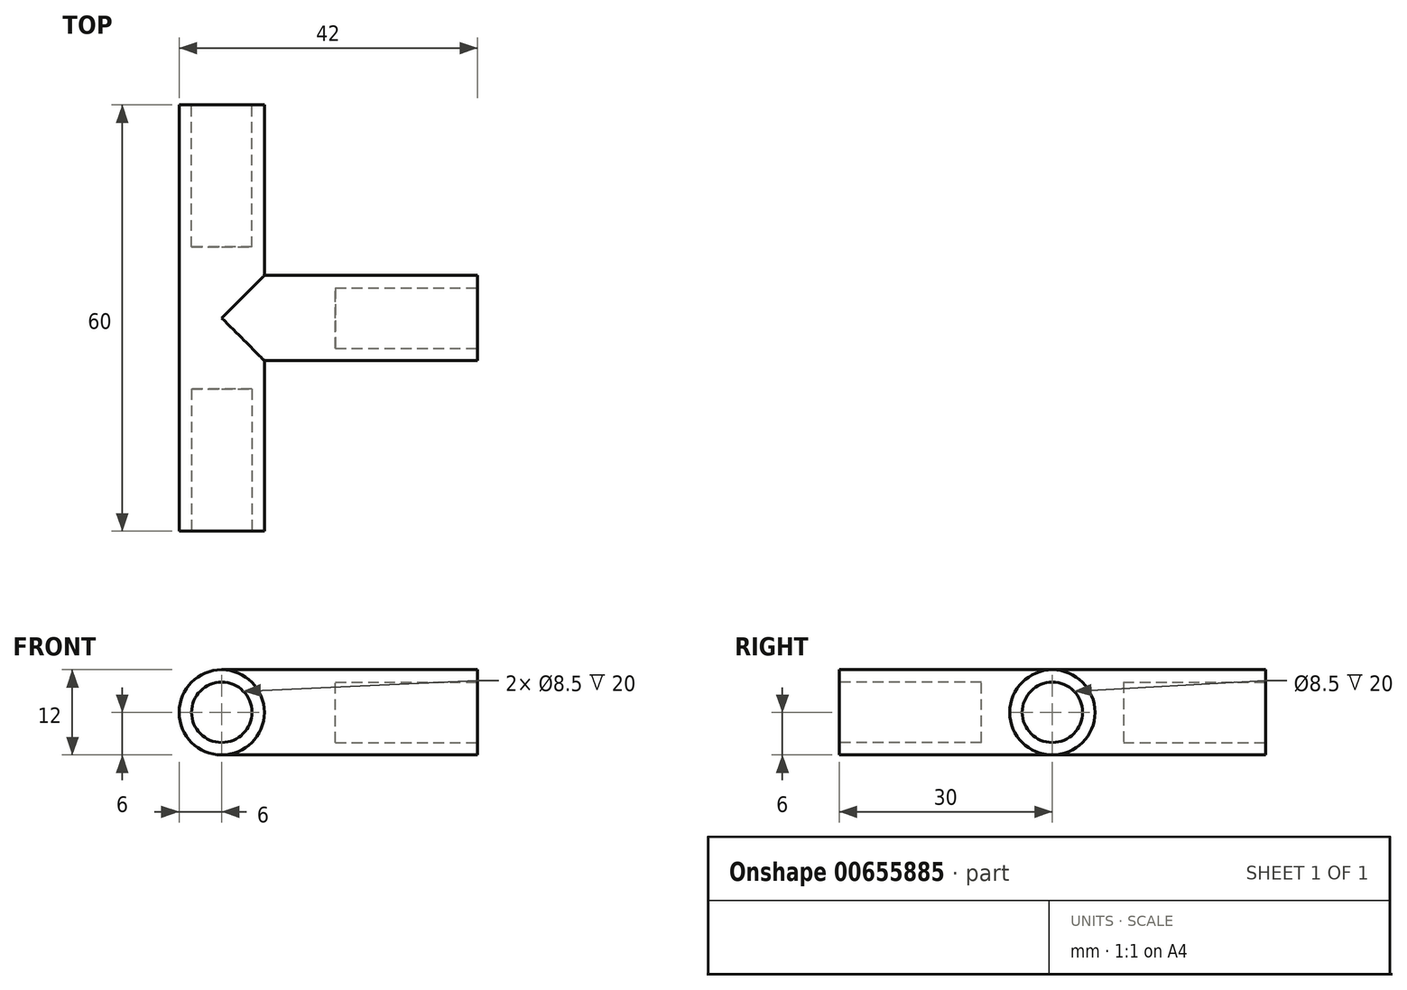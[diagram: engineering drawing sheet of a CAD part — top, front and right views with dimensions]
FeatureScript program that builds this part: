
annotation { "Feature Type Name" : "Feature", "Feature Type Description" : "" }
export const myFeature = defineFeature(function(context is Context, id is Id, definition is map)
    precondition{}
    {
        {
            var Q0;
            Q0=qCreatedBy(makeId("Top.planeOp"),FACE);
            var sketch = newSketch(context, id + "F0", { "sketchPlane" : qUnion([Q0])});
            skLineSegment(sketch, "E0.bottom", {"start": v(6, -30) * mm, "end": v(-6, -30) * mm});
            skLineSegment(sketch, "E0.top", {"start": v(6, 30) * mm, "end": v(-6, 30) * mm});
            skLineSegment(sketch, "E0.left", {"start": v(6, -30) * mm, "end": v(6, 30) * mm});
            skLineSegment(sketch, "E0.right", {"start": v(-6, -30) * mm, "end": v(-6, 30) * mm});
            skPoint(sketch, "E0.middle", {"position": v(0, 0) * mm});
            skLineSegment(sketch, "E1", {"start": v(6, 6) * mm, "end": v(36, 6) * mm});
            skLineSegment(sketch, "E2", {"start": v(0, 0) * mm, "end": v(210, 0) * mm});
            skLineSegment(sketch, "E3.MirrorCS", {"start": v(6, -6) * mm, "end": v(36, -6) * mm});
            skLineSegment(sketch, "E4", {"start": v(0, 6) * mm, "end": v(0, 30) * mm});
            skLineSegment(sketch, "E5", {"start": v(36, 6) * mm, "end": v(36, -6) * mm});
            skSolve(sketch);
        }
        {
            var Q0;
            {var subQ1=sQuery(id+"F0.wireOp",EDGE,"E0.bottom");Q0=makeQuery(id+"F0.imprint","IMPRINT",FACE,{"disambiguationData":[TD([[makeQuery(id+"F0.imprint","IMPRINT",EDGE,{"derivedFrom":subQ1}),-1.0]])]});}
            var Q1;
            {var subQ0=sQuery(id+"F0.wireOp",EDGE,"E1");Q1=makeQuery(id+"F0.imprint","IMPRINT",FACE,{"disambiguationData":[TD([[makeQuery(id+"F0.imprint","IMPRINT",EDGE,{"derivedFrom":subQ0}),-1.0]])]});}
            var Q2;
            {var subQ0=sQuery(id+"F0.wireOp",EDGE,"E3.MirrorCS");Q2=makeQuery(id+"F0.imprint","IMPRINT",FACE,{"disambiguationData":[TD([[makeQuery(id+"F0.imprint","IMPRINT",EDGE,{"derivedFrom":subQ0}),1.0]])]});}
            extrude(context, id + "F1", {"entities" : qUnion([Q0, Q1, Q2]), "depth" : 12 * mm, "offsetDistance" : 25 * mm});
        }
        {
            var Q0;
            Q0=makeQuery(id+"F1.opExtrude","SWEPT_FACE",FACE,{"disambiguationData":[OSD([sQuery(id+"F0.wireOp",EDGE,"E5")])]});
            var sketch = newSketch(context, id + "F2", { "sketchPlane" : qUnion([Q0])});
            skCircle(sketch, "E6", {"center": v(0, 6) * mm, "radius": 4.25 * mm});
            skPoint(sketch, "E6.centerSnap0", {"position": v(6, 6) * mm});
            skSolve(sketch);
        }
        {
            var Q0;
            Q0=makeQuery(id+"F1.opExtrude","SWEPT_FACE",FACE,{"disambiguationData":[OSD([sQuery(id+"F0.wireOp",EDGE,"E0.top")])]});
            var sketch = newSketch(context, id + "F3", { "sketchPlane" : qUnion([Q0])});
            skCircle(sketch, "E7", {"center": v(0, 6) * mm, "radius": 4.25 * mm});
            skPoint(sketch, "E7.centerSnap0", {"position": v(6, 6) * mm});
            skSolve(sketch);
        }
        {
            var Q0;
            Q0=makeQuery(id+"F1.opExtrude","SWEPT_FACE",FACE,{"disambiguationData":[OSD([sQuery(id+"F0.wireOp",EDGE,"E0.bottom")])]});
            var sketch = newSketch(context, id + "F4", { "sketchPlane" : qUnion([Q0])});
            skCircle(sketch, "E8", {"center": v(0, 6) * mm, "radius": 4.25 * mm});
            skPoint(sketch, "E8.centerSnap0", {"position": v(6, 6) * mm});
            skSolve(sketch);
        }
        {
            var Q0;
            Q0=makeQuery(id+"F3.imprint","IMPRINT",FACE,{"disambiguationData":[TD([[makeQuery(id+"F3.imprint","IMPRINT",EDGE,{"derivedFrom":sQuery(id+"F3.wireOp",EDGE,"E7")}),1.0]])]});
            extrude(context, id + "F5", {"entities" : qUnion([Q0]), "operationType" : NewBodyOperationType.REMOVE, "oppositeDirection" : true, "depth" : 20 * mm, "offsetDistance" : 25 * mm});
        }
        {
            var Q0;
            Q0=makeQuery(id+"F4.imprint","IMPRINT",FACE,{"disambiguationData":[TD([[makeQuery(id+"F4.imprint","IMPRINT",EDGE,{"derivedFrom":sQuery(id+"F4.wireOp",EDGE,"E8")}),1.0]])]});
            extrude(context, id + "F6", {"entities" : qUnion([Q0]), "operationType" : NewBodyOperationType.REMOVE, "oppositeDirection" : true, "depth" : 20 * mm, "offsetDistance" : 25 * mm});
        }
        {
            var Q0;
            Q0=makeQuery(id+"F2.imprint","IMPRINT",FACE,{"disambiguationData":[TD([[makeQuery(id+"F2.imprint","IMPRINT",EDGE,{"derivedFrom":sQuery(id+"F2.wireOp",EDGE,"E6")}),1.0]])]});
            extrude(context, id + "F7", {"entities" : qUnion([Q0]), "operationType" : NewBodyOperationType.REMOVE, "oppositeDirection" : true, "depth" : 20 * mm, "offsetDistance" : 25 * mm});
        }
        {
            var Q0;
            {var subQ0=sQuery(id+"F0.wireOp",EDGE,"E0.left");Q0=makeQuery(id+"F1.opExtrude","CAP_EDGE",EDGE,{"disambiguationData":[OSD([subQ0]),TDD([makeQuery(id+"F0.imprint","IMPRINT",EDGE,{"disambiguationData":[TD([[makeQuery(id+"F0.imprint","INTERSECT",VERTEX,{"derivedFrom":[sQuery(id+"F0.wireOp",EDGE,"E0.bottom"),subQ0]}),-1.0]])],"derivedFrom":subQ0})])],"isStart":false});}
            var Q1;
            Q1=makeQuery(id+"F1.opExtrude","CAP_EDGE",EDGE,{"disambiguationData":[OSD([sQuery(id+"F0.wireOp",EDGE,"E3.MirrorCS")])],"isStart":false});
            var Q2;
            Q2=makeQuery(id+"F1.opExtrude","CAP_EDGE",EDGE,{"disambiguationData":[OSD([sQuery(id+"F0.wireOp",EDGE,"E1")])],"isStart":false});
            var Q3;
            {var subQ0=sQuery(id+"F0.wireOp",EDGE,"E0.left");Q3=makeQuery(id+"F1.opExtrude","CAP_EDGE",EDGE,{"disambiguationData":[OSD([subQ0]),TDD([makeQuery(id+"F0.imprint","IMPRINT",EDGE,{"disambiguationData":[TD([[makeQuery(id+"F0.imprint","INTERSECT",VERTEX,{"derivedFrom":[sQuery(id+"F0.wireOp",EDGE,"E0.top"),subQ0]}),1.0]])],"derivedFrom":subQ0})])],"isStart":false});}
            var Q4;
            Q4=makeQuery(id+"F1.opExtrude","CAP_EDGE",EDGE,{"disambiguationData":[OSD([sQuery(id+"F0.wireOp",EDGE,"E0.right")])],"isStart":false});
            var Q5;
            Q5=makeQuery(id+"F1.opExtrude","CAP_EDGE",EDGE,{"disambiguationData":[OSD([sQuery(id+"F0.wireOp",EDGE,"E0.right")])],"isStart":true});
            var Q6;
            {var subQ0=sQuery(id+"F0.wireOp",EDGE,"E0.left");Q6=makeQuery(id+"F1.opExtrude","CAP_EDGE",EDGE,{"disambiguationData":[OSD([subQ0]),TDD([makeQuery(id+"F0.imprint","IMPRINT",EDGE,{"disambiguationData":[TD([[makeQuery(id+"F0.imprint","INTERSECT",VERTEX,{"derivedFrom":[sQuery(id+"F0.wireOp",EDGE,"E0.top"),subQ0]}),1.0]])],"derivedFrom":subQ0})])],"isStart":true});}
            var Q7;
            {var subQ0=sQuery(id+"F0.wireOp",EDGE,"E0.left");Q7=makeQuery(id+"F1.opExtrude","CAP_EDGE",EDGE,{"disambiguationData":[OSD([subQ0]),TDD([makeQuery(id+"F0.imprint","IMPRINT",EDGE,{"disambiguationData":[TD([[makeQuery(id+"F0.imprint","INTERSECT",VERTEX,{"derivedFrom":[sQuery(id+"F0.wireOp",EDGE,"E0.bottom"),subQ0]}),-1.0]])],"derivedFrom":subQ0})])],"isStart":true});}
            var Q8;
            Q8=makeQuery(id+"F1.opExtrude","CAP_EDGE",EDGE,{"disambiguationData":[OSD([sQuery(id+"F0.wireOp",EDGE,"E3.MirrorCS")])],"isStart":true});
            var Q9;
            Q9=makeQuery(id+"F1.opExtrude","CAP_EDGE",EDGE,{"disambiguationData":[OSD([sQuery(id+"F0.wireOp",EDGE,"E1")])],"isStart":true});
            fillet(context, id + "F8", {"entities" : qUnion([Q0, Q1, Q2, Q3, Q4, Q5, Q6, Q7, Q8, Q9]), "radius" : 6 * mm, "tangentPropagation" : true, "allowEdgeOverflow" : false});
        }
    });
